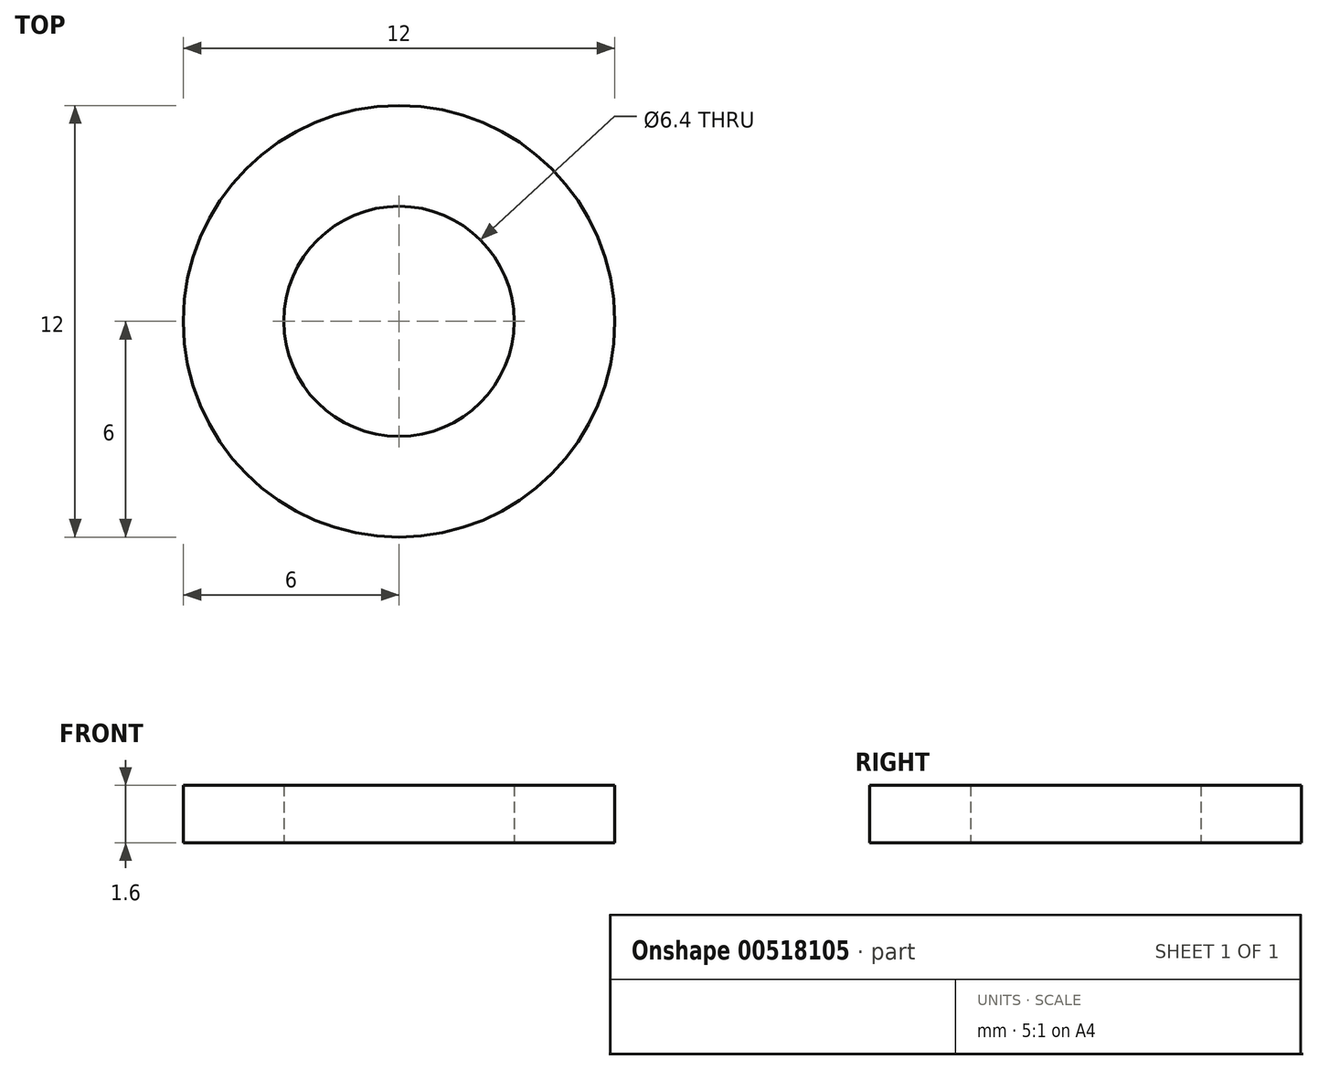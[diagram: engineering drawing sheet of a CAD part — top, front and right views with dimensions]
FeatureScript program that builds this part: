
annotation { "Feature Type Name" : "Feature", "Feature Type Description" : "" }
export const myFeature = defineFeature(function(context is Context, id is Id, definition is map)
    precondition{}
    {
        {
            assignVariable(context, id + "F0", {"name" : "s", "anyValue" : 1.6});
        }
        {
            var Q0;
            Q0=qCreatedBy(makeId("Top.planeOp"),FACE);
            var sketch = newSketch(context, id + "F1", { "sketchPlane" : qUnion([Q0])});
            skCircle(sketch, "E0", {"center": v(0, 0) * mm, "radius": 3.2 * mm});
            skCircle(sketch, "E1", {"center": v(0, 0) * mm, "radius": 6 * mm});
            skSolve(sketch);
        }
        {
            var Q0;
            Q0=makeQuery(id+"F1.imprint","IMPRINT",FACE,{"disambiguationData":[TD([[makeQuery(id+"F1.imprint","IMPRINT",EDGE,{"derivedFrom":sQuery(id+"F1.wireOp",EDGE,"E0")}),-1.0]])]});
            extrude(context, id + "F2", {"entities" : qUnion([Q0]), "depth" : (getVariable(context, 's')) * mm, "offsetDistance" : 25 * mm});
        }
    });
